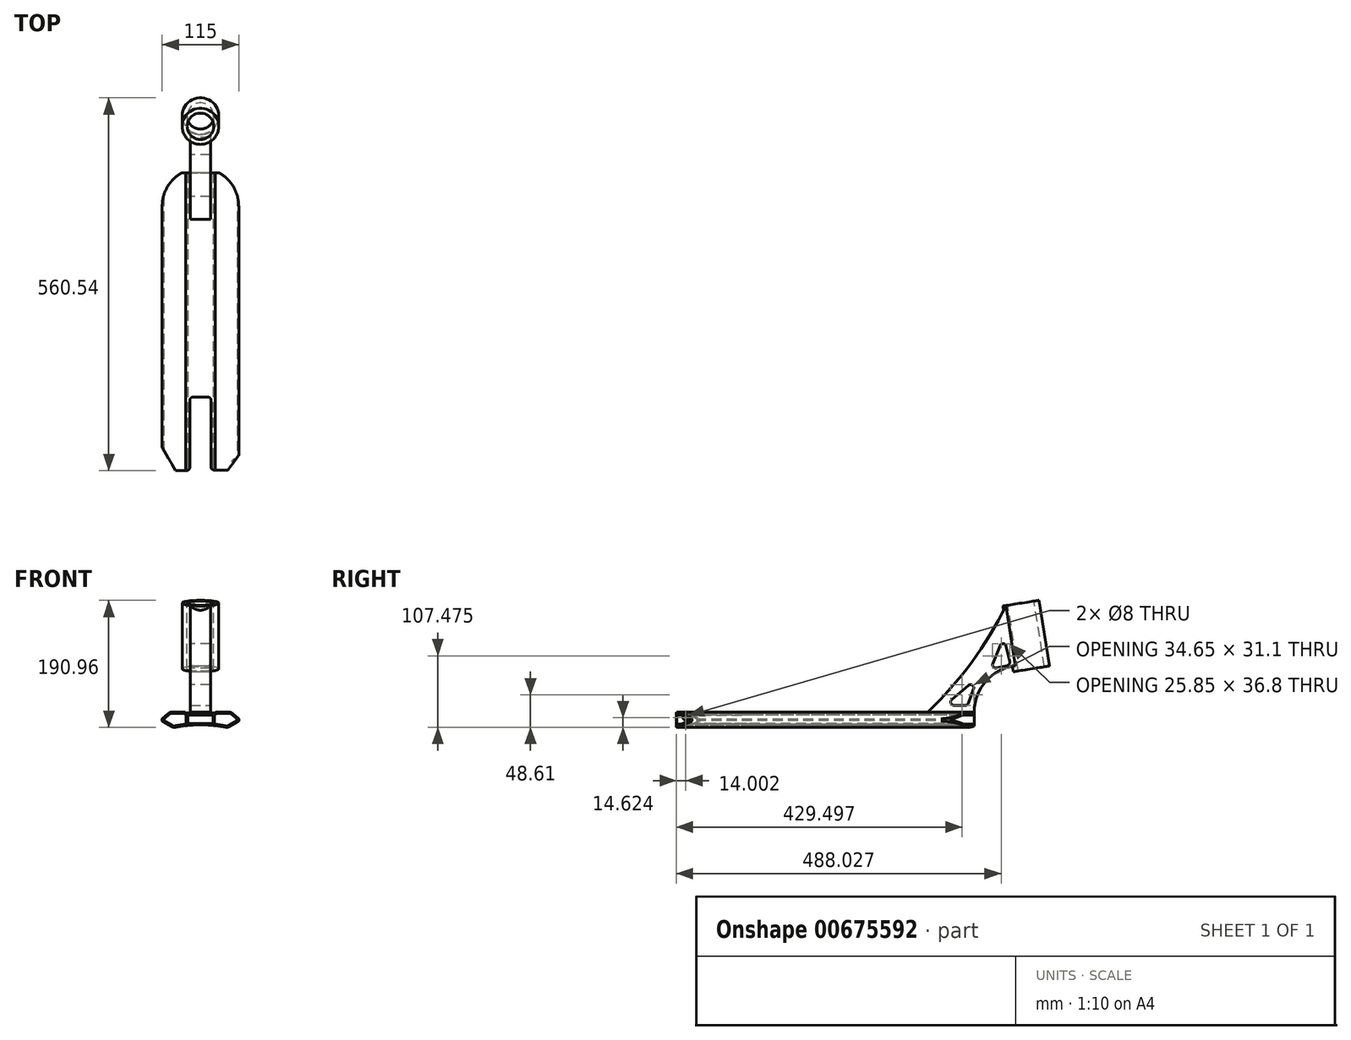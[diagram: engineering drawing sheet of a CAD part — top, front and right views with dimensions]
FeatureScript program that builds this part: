
annotation { "Feature Type Name" : "Feature", "Feature Type Description" : "" }
export const myFeature = defineFeature(function(context is Context, id is Id, definition is map)
    precondition{}
    {
        {
            var Q0;
            Q0=qCreatedBy(makeId("Front.planeOp"),FACE);
            var sketch = newSketch(context, id + "F0", { "sketchPlane" : qUnion([Q0])});
            skLineSegment(sketch, "E0", {"start": v(0, 43.55) * mm, "end": v(0, -57.48) * mm, "construction": true});
            skLineSegment(sketch, "E1", {"start": v(0, 0) * mm, "end": v(22.5, 0) * mm});
            skLineSegment(sketch, "E2", {"start": v(22.5, 0) * mm, "end": v(22.5, 1.3) * mm});
            skLineSegment(sketch, "E3", {"start": v(22.5, 1.3) * mm, "end": v(45.58, 1.3) * mm});
            skLineSegment(sketch, "E4", {"start": v(45.58, 1.3) * mm, "end": v(57.5, -8.7) * mm});
            skLineSegment(sketch, "E5", {"start": v(57.5, -8.7) * mm, "end": v(57.5, -12.7) * mm});
            skLineSegment(sketch, "E6", {"start": v(57.5, -12.7) * mm, "end": v(40.96, -22.25) * mm});
            skLineSegment(sketch, "E7.MirrorCS", {"start": v(0, 0) * mm, "end": v(-22.5, 0) * mm});
            skLineSegment(sketch, "E8.MirrorCS", {"start": v(-22.5, 0) * mm, "end": v(-22.5, 1.3) * mm});
            skLineSegment(sketch, "E9.MirrorCS", {"start": v(-22.5, 1.3) * mm, "end": v(-45.58, 1.3) * mm});
            skLineSegment(sketch, "E10.MirrorCS", {"start": v(-45.58, 1.3) * mm, "end": v(-57.5, -8.7) * mm});
            skLineSegment(sketch, "E11.MirrorCS", {"start": v(-57.5, -8.7) * mm, "end": v(-57.5, -12.7) * mm});
            skLineSegment(sketch, "E12.MirrorCS", {"start": v(-57.5, -12.7) * mm, "end": v(-40.96, -22.25) * mm});
            skArc(sketch, "E13", {"start": v(40.96, -22.25) * mm, "mid": v(0, -18.01) * mm, "end": v(-40.96, -22.25) * mm});
            skSolve(sketch);
        }
        {
            var Q0;
            Q0=makeQuery(id+"F0.imprint","IMPRINT",FACE,{"disambiguationData":[TD([[makeQuery(id+"F0.imprint","IMPRINT",EDGE,{"derivedFrom":sQuery(id+"F0.wireOp",EDGE,"E1")}),-1.0]])]});
            extrude(context, id + "F1", {"entities" : qUnion([Q0]), "endBound" : BoundingType.SYMMETRIC, "depth" : 500 * mm, "offsetDistance" : 25 * mm});
        }
        {
            var Q0;
            Q0=qCreatedBy(makeId("Front.planeOp"),FACE);
            var sketch = newSketch(context, id + "F2", { "sketchPlane" : qUnion([Q0])});
            skLineSegment(sketch, "E14.bottom", {"start": v(-19, -3.15) * mm, "end": v(19, -3.15) * mm});
            skLineSegment(sketch, "E14.top", {"start": v(-19, -16.15) * mm, "end": v(19, -16.15) * mm});
            skLineSegment(sketch, "E14.left", {"start": v(-19, -3.15) * mm, "end": v(-19, -16.15) * mm});
            skLineSegment(sketch, "E14.right", {"start": v(19, -3.15) * mm, "end": v(19, -16.15) * mm});
            skSolve(sketch);
        }
        {
            var Q0;
            Q0 = qSketchRegion(id + "F2", true);
            extrude(context, id + "F3", {"entities" : qUnion([Q0]), "operationType" : NewBodyOperationType.REMOVE, "endBound" : BoundingType.SYMMETRIC, "oppositeDirection" : true, "depth" : 500 * mm, "offsetDistance" : 25 * mm});
        }
        {
            var Q0;
            Q0=makeQuery(id+"F1.opExtrude","SWEPT_EDGE",EDGE,{"disambiguationData":[OSD([sQuery(id+"F0.wireOp",EDGE,"E8.MirrorCS"),sQuery(id+"F0.wireOp",EDGE,"E9.MirrorCS")])]});
            var Q1;
            Q1=makeQuery(id+"F1.opExtrude","SWEPT_EDGE",EDGE,{"disambiguationData":[OSD([sQuery(id+"F0.wireOp",EDGE,"E2"),sQuery(id+"F0.wireOp",EDGE,"E3")])]});
            fillet(context, id + "F4", {"entities" : qUnion([Q0, Q1]), "radius" : 2 * mm, "tangentPropagation" : true, "allowEdgeOverflow" : false});
        }
        {
            var Q0;
            Q0=makeQuery(id+"F1.opExtrude","SWEPT_EDGE",EDGE,{"disambiguationData":[OSD([sQuery(id+"F0.wireOp",EDGE,"E9.MirrorCS"),sQuery(id+"F0.wireOp",EDGE,"E10.MirrorCS")])]});
            var Q1;
            Q1=makeQuery(id+"F1.opExtrude","SWEPT_EDGE",EDGE,{"disambiguationData":[OSD([sQuery(id+"F0.wireOp",EDGE,"E3"),sQuery(id+"F0.wireOp",EDGE,"E4")])]});
            var Q2;
            Q2=makeQuery(id+"F1.opExtrude","SWEPT_EDGE",EDGE,{"disambiguationData":[OSD([sQuery(id+"F0.wireOp",EDGE,"E6"),sQuery(id+"F0.wireOp",EDGE,"E13")])]});
            var Q3;
            Q3=makeQuery(id+"F1.opExtrude","SWEPT_EDGE",EDGE,{"disambiguationData":[OSD([sQuery(id+"F0.wireOp",EDGE,"E12.MirrorCS"),sQuery(id+"F0.wireOp",EDGE,"E13")])]});
            fillet(context, id + "F5", {"entities" : qUnion([Q0, Q1, Q2, Q3]), "radius" : 9 * mm, "tangentPropagation" : true, "allowEdgeOverflow" : false});
        }
        {
            var Q0;
            Q0=makeQuery(id+"F1.opExtrude","SWEPT_EDGE",EDGE,{"disambiguationData":[OSD([sQuery(id+"F0.wireOp",EDGE,"E4"),sQuery(id+"F0.wireOp",EDGE,"E5")])]});
            var Q1;
            Q1=makeQuery(id+"F1.opExtrude","SWEPT_EDGE",EDGE,{"disambiguationData":[OSD([sQuery(id+"F0.wireOp",EDGE,"E5"),sQuery(id+"F0.wireOp",EDGE,"E6")])]});
            var Q2;
            Q2=makeQuery(id+"F1.opExtrude","SWEPT_EDGE",EDGE,{"disambiguationData":[OSD([sQuery(id+"F0.wireOp",EDGE,"E10.MirrorCS"),sQuery(id+"F0.wireOp",EDGE,"E11.MirrorCS")])]});
            var Q3;
            Q3=makeQuery(id+"F1.opExtrude","SWEPT_EDGE",EDGE,{"disambiguationData":[OSD([sQuery(id+"F0.wireOp",EDGE,"E11.MirrorCS"),sQuery(id+"F0.wireOp",EDGE,"E12.MirrorCS")])]});
            fillet(context, id + "F6", {"entities" : qUnion([Q0, Q1, Q2, Q3]), "radius" : 1 * mm, "tangentPropagation" : true, "allowEdgeOverflow" : false});
        }
        {
            var Q0;
            Q0=makeQuery(id+"F1.opExtrude","CAP_FACE",FACE,{"disambiguationData":[OSD([sQuery(id+"F0.wireOp",EDGE,"E1"),sQuery(id+"F0.wireOp",EDGE,"E2"),sQuery(id+"F0.wireOp",EDGE,"E3"),sQuery(id+"F0.wireOp",EDGE,"E4"),sQuery(id+"F0.wireOp",EDGE,"E5"),sQuery(id+"F0.wireOp",EDGE,"E6"),sQuery(id+"F0.wireOp",EDGE,"E7.MirrorCS"),sQuery(id+"F0.wireOp",EDGE,"E8.MirrorCS"),sQuery(id+"F0.wireOp",EDGE,"E9.MirrorCS"),sQuery(id+"F0.wireOp",EDGE,"E10.MirrorCS"),sQuery(id+"F0.wireOp",EDGE,"E11.MirrorCS"),sQuery(id+"F0.wireOp",EDGE,"E12.MirrorCS"),sQuery(id+"F0.wireOp",EDGE,"E13")])],"isStart":false});
            var sketch = newSketch(context, id + "F7", { "sketchPlane" : qUnion([Q0])});
            skLineSegment(sketch, "E15.0.0", {"start": v(43.9, -20.55) * mm, "end": v(57, -12.99) * mm});
            skArc(sketch, "E15.0.1", {"start": v(57, -12.99) * mm, "mid": v(57.37, -12.62) * mm, "end": v(57.5, -12.12) * mm});
            skLineSegment(sketch, "E15.0.2", {"start": v(57.5, -12.12) * mm, "end": v(57.5, -9.17) * mm});
            skArc(sketch, "E15.0.3", {"start": v(57.5, -9.17) * mm, "mid": v(57.4, -8.74) * mm, "end": v(57.14, -8.4) * mm});
            skLineSegment(sketch, "E15.0.4", {"start": v(57.14, -8.4) * mm, "end": v(48.1, -0.8) * mm});
            skArc(sketch, "E15.0.5", {"start": v(48.1, -0.8) * mm, "mid": v(45.38, 0.76) * mm, "end": v(42.3, 1.3) * mm});
            skLineSegment(sketch, "E15.0.6", {"start": v(42.3, 1.3) * mm, "end": v(24.37, 1.3) * mm});
            skArc(sketch, "E15.0.7", {"start": v(24.37, 1.3) * mm, "mid": v(23.23, 0.94) * mm, "end": v(22.5, 0) * mm});
            skLineSegment(sketch, "E15.0.8", {"start": v(22.5, 0) * mm, "end": v(-22.5, 0) * mm});
            skArc(sketch, "E15.0.9", {"start": v(-22.5, 0) * mm, "mid": v(-23.23, 0.94) * mm, "end": v(-24.37, 1.3) * mm});
            skLineSegment(sketch, "E15.0.10", {"start": v(-24.37, 1.3) * mm, "end": v(-42.3, 1.3) * mm});
            skArc(sketch, "E15.0.11", {"start": v(-42.3, 1.3) * mm, "mid": v(-45.38, 0.76) * mm, "end": v(-48.1, -0.8) * mm});
            skLineSegment(sketch, "E15.0.12", {"start": v(-48.1, -0.8) * mm, "end": v(-57.14, -8.4) * mm});
            skArc(sketch, "E15.0.13", {"start": v(-57.14, -8.4) * mm, "mid": v(-57.4, -8.74) * mm, "end": v(-57.5, -9.17) * mm});
            skLineSegment(sketch, "E15.0.14", {"start": v(-57.5, -9.17) * mm, "end": v(-57.5, -12.12) * mm});
            skArc(sketch, "E15.0.15", {"start": v(-57.5, -12.12) * mm, "mid": v(-57.37, -12.62) * mm, "end": v(-57, -12.99) * mm});
            skLineSegment(sketch, "E15.0.16", {"start": v(-57, -12.99) * mm, "end": v(-43.9, -20.55) * mm});
            skArc(sketch, "E15.0.17", {"start": v(-43.9, -20.55) * mm, "mid": v(-40.9, -21.63) * mm, "end": v(-37.7, -21.6) * mm});
            skArc(sketch, "E15.0.18", {"start": v(-37.7, -21.6) * mm, "mid": v(0, -18.01) * mm, "end": v(37.7, -21.6) * mm});
            skArc(sketch, "E15.0.19", {"start": v(37.7, -21.6) * mm, "mid": v(40.9, -21.63) * mm, "end": v(43.9, -20.55) * mm});
            skArc(sketch, "E16.0", {"start": v(-38.08, -19.63) * mm, "mid": v(0, -16.01) * mm, "end": v(38.08, -19.63) * mm});
            skArc(sketch, "E16.1", {"start": v(-42.9, -18.82) * mm, "mid": v(-40.56, -19.66) * mm, "end": v(-38.08, -19.63) * mm});
            skLineSegment(sketch, "E16.2", {"start": v(-55.5, -11.55) * mm, "end": v(-42.9, -18.82) * mm});
            skLineSegment(sketch, "E16.3", {"start": v(-55.5, -9.63) * mm, "end": v(-55.5, -11.55) * mm});
            skLineSegment(sketch, "E16.4", {"start": v(-24.37, -0.7) * mm, "end": v(-24.37, -0.7) * mm});
            skLineSegment(sketch, "E16.5", {"start": v(-24.37, -0.7) * mm, "end": v(-42.3, -0.7) * mm});
            skArc(sketch, "E16.6", {"start": v(-42.3, -0.7) * mm, "mid": v(-44.7, -1.12) * mm, "end": v(-46.8, -2.34) * mm});
            skLineSegment(sketch, "E16.7", {"start": v(-46.8, -2.34) * mm, "end": v(-55.5, -9.63) * mm});
            skLineSegment(sketch, "E17", {"start": v(-21.29, -17.14) * mm, "end": v(-21.29, -3.11) * mm});
            skLineSegment(sketch, "E18", {"start": v(-21.29, -3.11) * mm, "end": v(-22.42, -3.11) * mm});
            skArc(sketch, "E19", {"start": v(-22.42, -3.11) * mm, "mid": v(-22.82, -1.44) * mm, "end": v(-24.37, -0.7) * mm});
            skLineSegment(sketch, "E20.MirrorCS", {"start": v(24.37, -0.7) * mm, "end": v(42.3, -0.7) * mm});
            skLineSegment(sketch, "E21.MirrorCS", {"start": v(21.29, -17.14) * mm, "end": v(21.29, -3.11) * mm});
            skArc(sketch, "E22.MirrorCS", {"start": v(22.42, -3.11) * mm, "mid": v(22.82, -1.44) * mm, "end": v(24.37, -0.7) * mm});
            skArc(sketch, "E23.MirrorCS", {"start": v(42.3, -0.7) * mm, "mid": v(44.7, -1.12) * mm, "end": v(46.8, -2.34) * mm});
            skLineSegment(sketch, "E24.MirrorCS", {"start": v(46.8, -2.34) * mm, "end": v(55.5, -9.63) * mm});
            skLineSegment(sketch, "E25.MirrorCS", {"start": v(55.5, -9.63) * mm, "end": v(55.5, -11.55) * mm});
            skLineSegment(sketch, "E26.MirrorCS", {"start": v(55.5, -11.55) * mm, "end": v(42.9, -18.82) * mm});
            skArc(sketch, "E27.MirrorCS", {"start": v(42.9, -18.82) * mm, "mid": v(40.56, -19.66) * mm, "end": v(38.08, -19.63) * mm});
            skLineSegment(sketch, "E28.MirrorCS", {"start": v(21.29, -3.11) * mm, "end": v(22.42, -3.11) * mm});
            skSolve(sketch);
        }
        {
            var Q0;
            {var subQ0=sQuery(id+"F7.wireOp",EDGE,"E16.1");Q0=makeQuery(id+"F7.imprint","IMPRINT",FACE,{"disambiguationData":[TD([[makeQuery(id+"F7.imprint","IMPRINT",EDGE,{"derivedFrom":subQ0}),1.0]])]});}
            var Q1;
            Q1=makeQuery(id+"F7.imprint","IMPRINT",FACE,{"disambiguationData":[TD([[makeQuery(id+"F7.imprint","IMPRINT",EDGE,{"derivedFrom":sQuery(id+"F7.wireOp",EDGE,"E20.MirrorCS")}),-1.0]])]});
            extrude(context, id + "F8", {"entities" : qUnion([Q0, Q1]), "operationType" : NewBodyOperationType.REMOVE, "endBound" : BoundingType.THROUGH_ALL, "oppositeDirection" : true, "depth" : 25 * mm, "offsetDistance" : 25 * mm});
        }
        {
            var Q0;
            Q0=qCreatedBy(makeId("Top.planeOp"),FACE);
            var sketch = newSketch(context, id + "F9", { "sketchPlane" : qUnion([Q0])});
            skArc(sketch, "E29", {"start": v(57.5, 199.96) * mm, "mid": v(0, 257.5) * mm, "end": v(-57.5, 199.96) * mm});
            skLineSegment(sketch, "E30.bottom", {"start": v(57.5, 199.96) * mm, "end": v(-57.5, 199.96) * mm});
            skLineSegment(sketch, "E30.top", {"start": v(57.5, 279.96) * mm, "end": v(-57.5, 279.96) * mm});
            skLineSegment(sketch, "E30.left", {"start": v(57.5, 199.96) * mm, "end": v(57.5, 279.96) * mm});
            skLineSegment(sketch, "E30.right", {"start": v(-57.5, 199.96) * mm, "end": v(-57.5, 279.96) * mm});
            skSolve(sketch);
        }
        {
            var Q0;
            {var subQ0=sQuery(id+"F9.wireOp",EDGE,"E29");Q0=makeQuery(id+"F9.imprint","IMPRINT",FACE,{"disambiguationData":[TD([[makeQuery(id+"F9.imprint","IMPRINT",EDGE,{"derivedFrom":subQ0}),-1.0]])]});}
            extrude(context, id + "F10", {"entities" : qUnion([Q0]), "operationType" : NewBodyOperationType.REMOVE, "endBound" : BoundingType.THROUGH_ALL, "oppositeDirection" : true, "depth" : 25 * mm, "offsetDistance" : 25 * mm, "hasSecondDirection" : true, "secondDirectionBound" : SecondDirectionBoundingType.THROUGH_ALL, "secondDirectionOppositeDirection" : false, "secondDirectionDepth" : 25 * mm});
        }
        {
            var Q0;
            Q0=makeQuery(id+"F1.opExtrude","SWEPT_FACE",FACE,{"disambiguationData":[OSD([sQuery(id+"F0.wireOp",EDGE,"E1"),sQuery(id+"F0.wireOp",EDGE,"E7.MirrorCS")])]});
            var sketch = newSketch(context, id + "F11", { "sketchPlane" : qUnion([Q0])});
            skLineSegment(sketch, "E31", {"start": v(-37.3, -197.64) * mm, "end": v(-16, -197.64) * mm});
            skLineSegment(sketch, "E32", {"start": v(-16, -197.64) * mm, "end": v(-16, -86.98) * mm});
            skLineSegment(sketch, "E33", {"start": v(-16, -86.98) * mm, "end": v(16, -86.98) * mm});
            skLineSegment(sketch, "E34", {"start": v(16, -86.98) * mm, "end": v(16, -196.98) * mm});
            skLineSegment(sketch, "E35", {"start": v(16, -196.98) * mm, "end": v(41.12, -196.98) * mm});
            skLineSegment(sketch, "E36", {"start": v(41.12, -196.98) * mm, "end": v(68, -159.98) * mm});
            skLineSegment(sketch, "E37", {"start": v(68, -159.98) * mm, "end": v(68, -290.64) * mm});
            skLineSegment(sketch, "E38", {"start": v(68, -290.64) * mm, "end": v(-68, -290.64) * mm});
            skLineSegment(sketch, "E39", {"start": v(-68, -290.64) * mm, "end": v(-58.66, -160.64) * mm});
            skLineSegment(sketch, "E40", {"start": v(-58.66, -160.64) * mm, "end": v(-37.3, -197.64) * mm});
            skLineSegment(sketch, "E41", {"start": v(0, 0) * mm, "end": v(0, -329.97) * mm});
            skSolve(sketch);
        }
        {
            var Q0;
            Q0 = qSketchRegion(id + "F11", true);
            extrude(context, id + "F12", {"entities" : qUnion([Q0]), "operationType" : NewBodyOperationType.REMOVE, "endBound" : BoundingType.THROUGH_ALL, "oppositeDirection" : true, "depth" : 25 * mm, "offsetDistance" : 25 * mm, "hasSecondDirection" : true, "secondDirectionBound" : SecondDirectionBoundingType.THROUGH_ALL, "secondDirectionOppositeDirection" : false, "secondDirectionDepth" : 25 * mm});
        }
        {
            var Q0;
            {var subQ0=sQuery(id+"F11.wireOp",EDGE,"E33");var subQ1=sQuery(id+"F11.wireOp",EDGE,"E32");Q0=makeQuery(id+"F12.boolean.opBoolean","COPY",EDGE,{"disambiguationData":[TD([makeQuery(id+"F3.boolean.opBoolean","COPY",FACE,{"derivedFrom":makeQuery(id+"F3.opExtrude","SWEPT_FACE",FACE,{"disambiguationData":[OSD([sQuery(id+"F2.wireOp",EDGE,"E14.bottom")])]})})])],"derivedFrom":makeQuery(id+"F12.opExtrude","SWEPT_EDGE",EDGE,{"disambiguationData":[OSD([subQ1,subQ0])]})});}
            var Q1;
            {var subQ0=sQuery(id+"F11.wireOp",EDGE,"E33");var subQ1=sQuery(id+"F11.wireOp",EDGE,"E34");Q1=makeQuery(id+"F12.boolean.opBoolean","COPY",EDGE,{"disambiguationData":[TD([makeQuery(id+"F3.boolean.opBoolean","COPY",FACE,{"derivedFrom":makeQuery(id+"F3.opExtrude","SWEPT_FACE",FACE,{"disambiguationData":[OSD([sQuery(id+"F2.wireOp",EDGE,"E14.bottom")])]})})])],"derivedFrom":makeQuery(id+"F12.opExtrude","SWEPT_EDGE",EDGE,{"disambiguationData":[OSD([subQ0,subQ1])]})});}
            var Q2;
            {var subQ0=sQuery(id+"F11.wireOp",EDGE,"E31");var subQ1=sQuery(id+"F11.wireOp",EDGE,"E32");Q2=makeQuery(id+"F12.boolean.opBoolean","COPY",EDGE,{"disambiguationData":[TD([makeQuery(id+"F3.boolean.opBoolean","COPY",FACE,{"derivedFrom":makeQuery(id+"F3.opExtrude","SWEPT_FACE",FACE,{"disambiguationData":[OSD([sQuery(id+"F2.wireOp",EDGE,"E14.bottom")])]})})])],"derivedFrom":makeQuery(id+"F12.opExtrude","SWEPT_EDGE",EDGE,{"disambiguationData":[OSD([subQ0,subQ1])]})});}
            var Q3;
            {var subQ0=sQuery(id+"F11.wireOp",EDGE,"E31");var subQ1=sQuery(id+"F11.wireOp",EDGE,"E32");Q3=makeQuery(id+"F12.boolean.opBoolean","COPY",EDGE,{"disambiguationData":[TD([makeQuery(id+"F1.opExtrude","SWEPT_FACE",FACE,{"disambiguationData":[OSD([sQuery(id+"F0.wireOp",EDGE,"E13")])]})])],"derivedFrom":makeQuery(id+"F12.opExtrude","SWEPT_EDGE",EDGE,{"disambiguationData":[OSD([subQ0,subQ1])]})});}
            var Q4;
            {var subQ0=sQuery(id+"F11.wireOp",EDGE,"E32");var subQ1=sQuery(id+"F11.wireOp",EDGE,"E33");Q4=makeQuery(id+"F12.boolean.opBoolean","COPY",EDGE,{"disambiguationData":[TD([makeQuery(id+"F1.opExtrude","SWEPT_FACE",FACE,{"disambiguationData":[OSD([sQuery(id+"F0.wireOp",EDGE,"E13")])]})])],"derivedFrom":makeQuery(id+"F12.opExtrude","SWEPT_EDGE",EDGE,{"disambiguationData":[OSD([subQ0,subQ1])]})});}
            var Q5;
            {var subQ0=sQuery(id+"F11.wireOp",EDGE,"E34");var subQ1=sQuery(id+"F11.wireOp",EDGE,"E33");Q5=makeQuery(id+"F12.boolean.opBoolean","COPY",EDGE,{"disambiguationData":[TD([makeQuery(id+"F1.opExtrude","SWEPT_FACE",FACE,{"disambiguationData":[OSD([sQuery(id+"F0.wireOp",EDGE,"E13")])]})])],"derivedFrom":makeQuery(id+"F12.opExtrude","SWEPT_EDGE",EDGE,{"disambiguationData":[OSD([subQ1,subQ0])]})});}
            var Q6;
            {var subQ0=sQuery(id+"F11.wireOp",EDGE,"E34");var subQ1=sQuery(id+"F11.wireOp",EDGE,"E35");Q6=makeQuery(id+"F12.boolean.opBoolean","COPY",EDGE,{"disambiguationData":[TD([makeQuery(id+"F1.opExtrude","SWEPT_FACE",FACE,{"disambiguationData":[OSD([sQuery(id+"F0.wireOp",EDGE,"E13")])]})])],"derivedFrom":makeQuery(id+"F12.opExtrude","SWEPT_EDGE",EDGE,{"disambiguationData":[OSD([subQ0,subQ1])]})});}
            var Q7;
            {var subQ0=sQuery(id+"F11.wireOp",EDGE,"E35");var subQ1=sQuery(id+"F11.wireOp",EDGE,"E34");Q7=makeQuery(id+"F12.boolean.opBoolean","COPY",EDGE,{"disambiguationData":[TD([makeQuery(id+"F3.boolean.opBoolean","COPY",FACE,{"derivedFrom":makeQuery(id+"F3.opExtrude","SWEPT_FACE",FACE,{"disambiguationData":[OSD([sQuery(id+"F2.wireOp",EDGE,"E14.bottom")])]})})])],"derivedFrom":makeQuery(id+"F12.opExtrude","SWEPT_EDGE",EDGE,{"disambiguationData":[OSD([subQ1,subQ0])]})});}
            fillet(context, id + "F13", {"entities" : qUnion([Q0, Q1, Q2, Q3, Q4, Q5, Q6, Q7]), "radius" : 5 * mm, "tangentPropagation" : true, "allowEdgeOverflow" : false});
        }
        {
            var Q0;
            Q0=qCreatedBy(makeId("Right.planeOp"),FACE);
            var sketch = newSketch(context, id + "F14", { "sketchPlane" : qUnion([Q0])});
            skLineSegment(sketch, "E42", {"start": v(180, 1.3) * mm, "end": v(250, 1.3) * mm});
            skArc(sketch, "E43", {"start": v(180, 1.3) * mm, "mid": v(245.97, 75.96) * mm, "end": v(297.38, 161.3) * mm});
            skArc(sketch, "E44", {"start": v(311.71, 70.8) * mm, "mid": v(267.66, 47.78) * mm, "end": v(250, 1.3) * mm});
            skLineSegment(sketch, "E45", {"start": v(311.71, 70.8) * mm, "end": v(313.03, 62.53) * mm});
            skLineSegment(sketch, "E46", {"start": v(313.03, 62.53) * mm, "end": v(358.46, 69.73) * mm});
            skLineSegment(sketch, "E47", {"start": v(358.46, 69.73) * mm, "end": v(342.82, 168.5) * mm});
            skLineSegment(sketch, "E48", {"start": v(342.82, 168.5) * mm, "end": v(297.38, 161.3) * mm});
            skSolve(sketch);
        }
        {
            var Q0;
            Q0=makeQuery(id+"F14.imprint","IMPRINT",FACE,{"disambiguationData":[TD([[makeQuery(id+"F14.imprint","IMPRINT",EDGE,{"derivedFrom":sQuery(id+"F14.wireOp",EDGE,"E42")}),1.0]])]});
            extrude(context, id + "F15", {"entities" : qUnion([Q0]), "operationType" : NewBodyOperationType.ADD, "endBound" : BoundingType.SYMMETRIC, "depth" : 30 * mm, "offsetDistance" : 25 * mm});
        }
        {
            var Q0;
            Q0=makeQuery(id+"F15.opExtrude","SWEPT_FACE",FACE,{"disambiguationData":[OSD([sQuery(id+"F14.wireOp",EDGE,"E48")])]});
            var sketch = newSketch(context, id + "F16", { "sketchPlane" : qUnion([Q0])});
            skCircle(sketch, "E49", {"center": v(0, 341.95) * mm, "radius": 27.5 * mm});
            skSolve(sketch);
        }
        {
            var Q0;
            Q0 = qSketchRegion(id + "F16", true);
            var Q1;
            Q1=makeQuery(id+"F15.opExtrude","SWEPT_FACE",FACE,{"disambiguationData":[OSD([sQuery(id+"F14.wireOp",EDGE,"E46")])]});
            extrude(context, id + "F17", {"entities" : qUnion([Q0]), "operationType" : NewBodyOperationType.ADD, "endBound" : BoundingType.UP_TO_SURFACE, "oppositeDirection" : true, "depth" : 25 * mm, "endBoundEntityFace" : qUnion([Q1]), "offsetDistance" : 25 * mm});
        }
        {
            var Q0;
            Q0=makeQuery(id+"F17.boolean.opBoolean","MERGE",FACE,{"derivedFrom":[makeQuery(id+"F15.opExtrude","SWEPT_FACE",FACE,{"disambiguationData":[OSD([sQuery(id+"F14.wireOp",EDGE,"E48")])]}),makeQuery(id+"F17.opExtrude","CAP_FACE",FACE,{"disambiguationData":[OSD([sQuery(id+"F16.wireOp",EDGE,"E49")])],"isStart":true})]});
            var sketch = newSketch(context, id + "F18", { "sketchPlane" : qUnion([Q0])});
            skPoint(sketch, "E50", {"position": v(0, 341.95) * mm});
            skSolve(sketch);
        }
        {
            var Q0;
            Q0=sQuery(id+"F18.wireOp",VERTEX,"E50");
            var Q1;
            Q1=makeQuery(id+"F15.opExtrude","SWEPT_BODY",BODY,{"disambiguationData":[OSD([sQuery(id+"F14.wireOp",EDGE,"E42"),sQuery(id+"F14.wireOp",EDGE,"E43"),sQuery(id+"F14.wireOp",EDGE,"E44"),sQuery(id+"F14.wireOp",EDGE,"E45"),sQuery(id+"F14.wireOp",EDGE,"E46"),sQuery(id+"F14.wireOp",EDGE,"E47"),sQuery(id+"F14.wireOp",EDGE,"E48")])]});
            hole(context, id + "F19", {"style" : HoleStyle.SIMPLE, "endStyle" : HoleEndStyle.THROUGH, "holeDiameter" : 40 * mm, "majorDiameter" : 5 * mm, "isTappedThrough" : true, "tappedDepth" : 12 * mm, "tapClearance" : 3, "locations" : qUnion([Q0]), "scope" : qUnion([Q1])});
        }
        {
            var Q0;
            Q0=makeQuery(id+"F8.boolean.opBoolean","COPY",FACE,{"derivedFrom":makeQuery(id+"F8.opExtrude","SWEPT_FACE",FACE,{"disambiguationData":[OSD([sQuery(id+"F7.wireOp",EDGE,"E17")])]})});
            var sketch = newSketch(context, id + "F20", { "sketchPlane" : qUnion([Q0])});
            skPoint(sketch, "E51", {"position": v(183.64, -7.14) * mm});
            skSolve(sketch);
        }
        {
            var Q0;
            Q0=sQuery(id+"F20.wireOp",VERTEX,"E51");
            var Q1;
            Q1=makeQuery(id+"F1.opExtrude","SWEPT_BODY",BODY,{"disambiguationData":[OSD([sQuery(id+"F0.wireOp",EDGE,"E1"),sQuery(id+"F0.wireOp",EDGE,"E2"),sQuery(id+"F0.wireOp",EDGE,"E3"),sQuery(id+"F0.wireOp",EDGE,"E4"),sQuery(id+"F0.wireOp",EDGE,"E5"),sQuery(id+"F0.wireOp",EDGE,"E6"),sQuery(id+"F0.wireOp",EDGE,"E7.MirrorCS"),sQuery(id+"F0.wireOp",EDGE,"E8.MirrorCS"),sQuery(id+"F0.wireOp",EDGE,"E9.MirrorCS"),sQuery(id+"F0.wireOp",EDGE,"E10.MirrorCS"),sQuery(id+"F0.wireOp",EDGE,"E11.MirrorCS"),sQuery(id+"F0.wireOp",EDGE,"E12.MirrorCS"),sQuery(id+"F0.wireOp",EDGE,"E13")])]});
            hole(context, id + "F21", {"style" : HoleStyle.SIMPLE, "endStyle" : HoleEndStyle.THROUGH, "holeDiameter" : 8 * mm, "majorDiameter" : 5 * mm, "isTappedThrough" : true, "tappedDepth" : 12 * mm, "tapClearance" : 3, "locations" : qUnion([Q0]), "scope" : qUnion([Q1])});
        }
        {
            var Q0;
            Q0=makeQuery(id+"F15.opExtrude","CAP_FACE",FACE,{"disambiguationData":[OSD([sQuery(id+"F14.wireOp",EDGE,"E42"),sQuery(id+"F14.wireOp",EDGE,"E43"),sQuery(id+"F14.wireOp",EDGE,"E44"),sQuery(id+"F14.wireOp",EDGE,"E45"),sQuery(id+"F14.wireOp",EDGE,"E46"),sQuery(id+"F14.wireOp",EDGE,"E47"),sQuery(id+"F14.wireOp",EDGE,"E48")])],"isStart":false});
            var sketch = newSketch(context, id + "F22", { "sketchPlane" : qUnion([Q0])});
            skLineSegment(sketch, "E52", {"start": v(274.3, 65.34) * mm, "end": v(304.3, 72.12) * mm});
            skLineSegment(sketch, "E53", {"start": v(304.3, 72.12) * mm, "end": v(294.38, 116.01) * mm});
            skPoint(sketch, "E53.endSnap0", {"position": v(304.5, 116.01) * mm});
            skLineSegment(sketch, "E54", {"start": v(294.38, 116.01) * mm, "end": v(274.3, 65.34) * mm});
            skLineSegment(sketch, "E55", {"start": v(206, 11.3) * mm, "end": v(240, 11.3) * mm});
            skLineSegment(sketch, "E56", {"start": v(240, 11.3) * mm, "end": v(255.4, 53.59) * mm});
            skLineSegment(sketch, "E57", {"start": v(255.4, 53.59) * mm, "end": v(206, 11.3) * mm});
            skSolve(sketch);
        }
        {
            var Q0;
            Q0=makeQuery(id+"F22.imprint","IMPRINT",FACE,{"disambiguationData":[TD([[makeQuery(id+"F22.imprint","IMPRINT",EDGE,{"derivedFrom":sQuery(id+"F22.wireOp",EDGE,"E55")}),1.0]])]});
            var Q1;
            Q1=makeQuery(id+"F22.imprint","IMPRINT",FACE,{"disambiguationData":[TD([[makeQuery(id+"F22.imprint","IMPRINT",EDGE,{"derivedFrom":sQuery(id+"F22.wireOp",EDGE,"E52")}),1.0]])]});
            extrude(context, id + "F23", {"entities" : qUnion([Q0, Q1]), "operationType" : NewBodyOperationType.REMOVE, "endBound" : BoundingType.THROUGH_ALL, "oppositeDirection" : true, "depth" : 25 * mm, "offsetDistance" : 25 * mm});
        }
        {
            var Q0;
            Q0=makeQuery(id+"F23.boolean.opBoolean","COPY",EDGE,{"derivedFrom":makeQuery(id+"F23.opExtrude","SWEPT_EDGE",EDGE,{"disambiguationData":[OSD([sQuery(id+"F22.wireOp",EDGE,"E55"),sQuery(id+"F22.wireOp",EDGE,"E57")])]})});
            var Q1;
            Q1=makeQuery(id+"F23.boolean.opBoolean","COPY",EDGE,{"derivedFrom":makeQuery(id+"F23.opExtrude","SWEPT_EDGE",EDGE,{"disambiguationData":[OSD([sQuery(id+"F22.wireOp",EDGE,"E56"),sQuery(id+"F22.wireOp",EDGE,"E57")])]})});
            var Q2;
            Q2=makeQuery(id+"F23.boolean.opBoolean","COPY",EDGE,{"derivedFrom":makeQuery(id+"F23.opExtrude","SWEPT_EDGE",EDGE,{"disambiguationData":[OSD([sQuery(id+"F22.wireOp",EDGE,"E55"),sQuery(id+"F22.wireOp",EDGE,"E56")])]})});
            var Q3;
            Q3=makeQuery(id+"F23.boolean.opBoolean","COPY",EDGE,{"derivedFrom":makeQuery(id+"F23.opExtrude","SWEPT_EDGE",EDGE,{"disambiguationData":[OSD([sQuery(id+"F22.wireOp",EDGE,"E52"),sQuery(id+"F22.wireOp",EDGE,"E54")])]})});
            var Q4;
            Q4=makeQuery(id+"F23.boolean.opBoolean","COPY",EDGE,{"derivedFrom":makeQuery(id+"F23.opExtrude","SWEPT_EDGE",EDGE,{"disambiguationData":[OSD([sQuery(id+"F22.wireOp",EDGE,"E53"),sQuery(id+"F22.wireOp",EDGE,"E54")])]})});
            var Q5;
            Q5=makeQuery(id+"F23.boolean.opBoolean","COPY",EDGE,{"derivedFrom":makeQuery(id+"F23.opExtrude","SWEPT_EDGE",EDGE,{"disambiguationData":[OSD([sQuery(id+"F22.wireOp",EDGE,"E52"),sQuery(id+"F22.wireOp",EDGE,"E53")])]})});
            fillet(context, id + "F24", {"entities" : qUnion([Q0, Q1, Q2, Q3, Q4, Q5]), "radius" : 5 * mm, "tangentPropagation" : true, "allowEdgeOverflow" : false});
        }
    });
